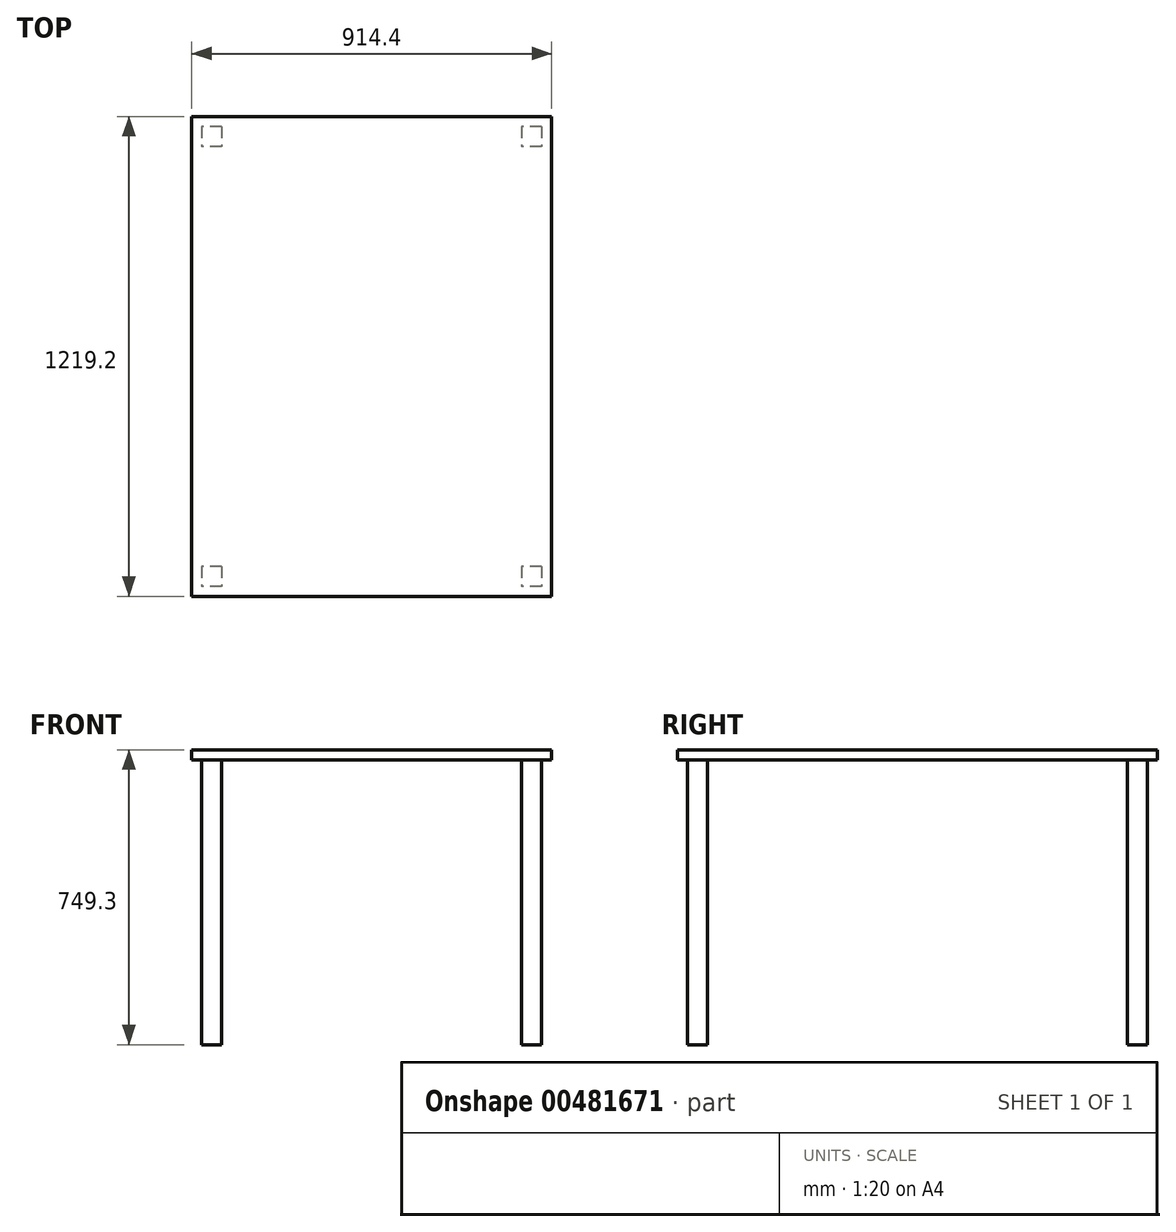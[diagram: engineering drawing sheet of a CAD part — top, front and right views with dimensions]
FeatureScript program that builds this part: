
annotation { "Feature Type Name" : "Feature", "Feature Type Description" : "" }
export const myFeature = defineFeature(function(context is Context, id is Id, definition is map)
    precondition{}
    {
        {
            var Q0;
            Q0=qCreatedBy(makeId("Top.planeOp"),FACE);
            var sketch = newSketch(context, id + "F0", { "sketchPlane" : qUnion([Q0])});
            skLineSegment(sketch, "E0.bottom", {"start": v(457.2, 609.6) * mm, "end": v(-457.2, 609.6) * mm});
            skLineSegment(sketch, "E0.top", {"start": v(457.2, -609.6) * mm, "end": v(-457.2, -609.6) * mm});
            skLineSegment(sketch, "E0.left", {"start": v(457.2, 609.6) * mm, "end": v(457.2, -609.6) * mm});
            skLineSegment(sketch, "E0.right", {"start": v(-457.2, 609.6) * mm, "end": v(-457.2, -609.6) * mm});
            skPoint(sketch, "E0.middle", {"position": v(0, 0) * mm});
            skSolve(sketch);
        }
        {
            var Q0;
            Q0=makeQuery(id+"F0.imprint","IMPRINT",FACE,{"disambiguationData":[TD([[makeQuery(id+"F0.imprint","IMPRINT",EDGE,{"derivedFrom":sQuery(id+"F0.wireOp",EDGE,"E0.bottom")}),1.0]])]});
            extrude(context, id + "F1", {"entities" : qUnion([Q0]), "depth" : 25.4 * mm});
        }
        {
            var Q0;
            Q0=makeQuery(id+"F1.opExtrude","CAP_FACE",FACE,{"disambiguationData":[OSD([sQuery(id+"F0.wireOp",EDGE,"E0.bottom"),sQuery(id+"F0.wireOp",EDGE,"E0.top"),sQuery(id+"F0.wireOp",EDGE,"E0.left"),sQuery(id+"F0.wireOp",EDGE,"E0.right")])],"isStart":true});
            var sketch = newSketch(context, id + "F2", { "sketchPlane" : qUnion([Q0])});
            skLineSegment(sketch, "E1.bottom", {"start": v(-381, 533.4) * mm, "end": v(-431.8, 533.4) * mm});
            skLineSegment(sketch, "E1.top", {"start": v(-381, 584.2) * mm, "end": v(-431.8, 584.2) * mm});
            skLineSegment(sketch, "E1.left", {"start": v(-381, 533.4) * mm, "end": v(-381, 584.2) * mm});
            skLineSegment(sketch, "E1.right", {"start": v(-431.8, 533.4) * mm, "end": v(-431.8, 584.2) * mm});
            skPoint(sketch, "E1.middle", {"position": v(-406.4, 558.8) * mm});
            skLineSegment(sketch, "E2.0.1.0", {"start": v(-431.8, -584.2) * mm, "end": v(-431.8, -533.4) * mm});
            skLineSegment(sketch, "E2.0.1.1", {"start": v(-381, -584.2) * mm, "end": v(-381, -533.4) * mm});
            skLineSegment(sketch, "E2.0.1.2", {"start": v(-381, -533.4) * mm, "end": v(-431.8, -533.4) * mm});
            skLineSegment(sketch, "E2.0.1.3", {"start": v(-381, -584.2) * mm, "end": v(-431.8, -584.2) * mm});
            skPoint(sketch, "E2.0.1.4", {"position": v(-406.4, -558.8) * mm});
            skLineSegment(sketch, "E2.1.0.0", {"start": v(381, 533.4) * mm, "end": v(381, 584.2) * mm});
            skLineSegment(sketch, "E2.1.0.1", {"start": v(431.8, 533.4) * mm, "end": v(431.8, 584.2) * mm});
            skLineSegment(sketch, "E2.1.0.2", {"start": v(431.8, 584.2) * mm, "end": v(381, 584.2) * mm});
            skLineSegment(sketch, "E2.1.0.3", {"start": v(431.8, 533.4) * mm, "end": v(381, 533.4) * mm});
            skPoint(sketch, "E2.1.0.4", {"position": v(406.4, 558.8) * mm});
            skLineSegment(sketch, "E2.1.1.0", {"start": v(381, -584.2) * mm, "end": v(381, -533.4) * mm});
            skLineSegment(sketch, "E2.1.1.1", {"start": v(431.8, -584.2) * mm, "end": v(431.8, -533.4) * mm});
            skLineSegment(sketch, "E2.1.1.2", {"start": v(431.8, -533.4) * mm, "end": v(381, -533.4) * mm});
            skLineSegment(sketch, "E2.1.1.3", {"start": v(431.8, -584.2) * mm, "end": v(381, -584.2) * mm});
            skPoint(sketch, "E2.1.1.4", {"position": v(406.4, -558.8) * mm});
            skLineSegment(sketch, "E2.direction1", {"start": v(-431.8, 533.4) * mm, "end": v(381, 533.4) * mm, "construction": true});
            skLineSegment(sketch, "E2.direction2", {"start": v(-431.8, 533.4) * mm, "end": v(-431.8, -584.2) * mm, "construction": true});
            skSolve(sketch);
        }
        {
            var Q0;
            Q0 = qSketchRegion(id + "F2", true);
            extrude(context, id + "F3", {"entities" : qUnion([Q0]), "operationType" : NewBodyOperationType.ADD, "depth" : 723.9 * mm});
        }
    });
